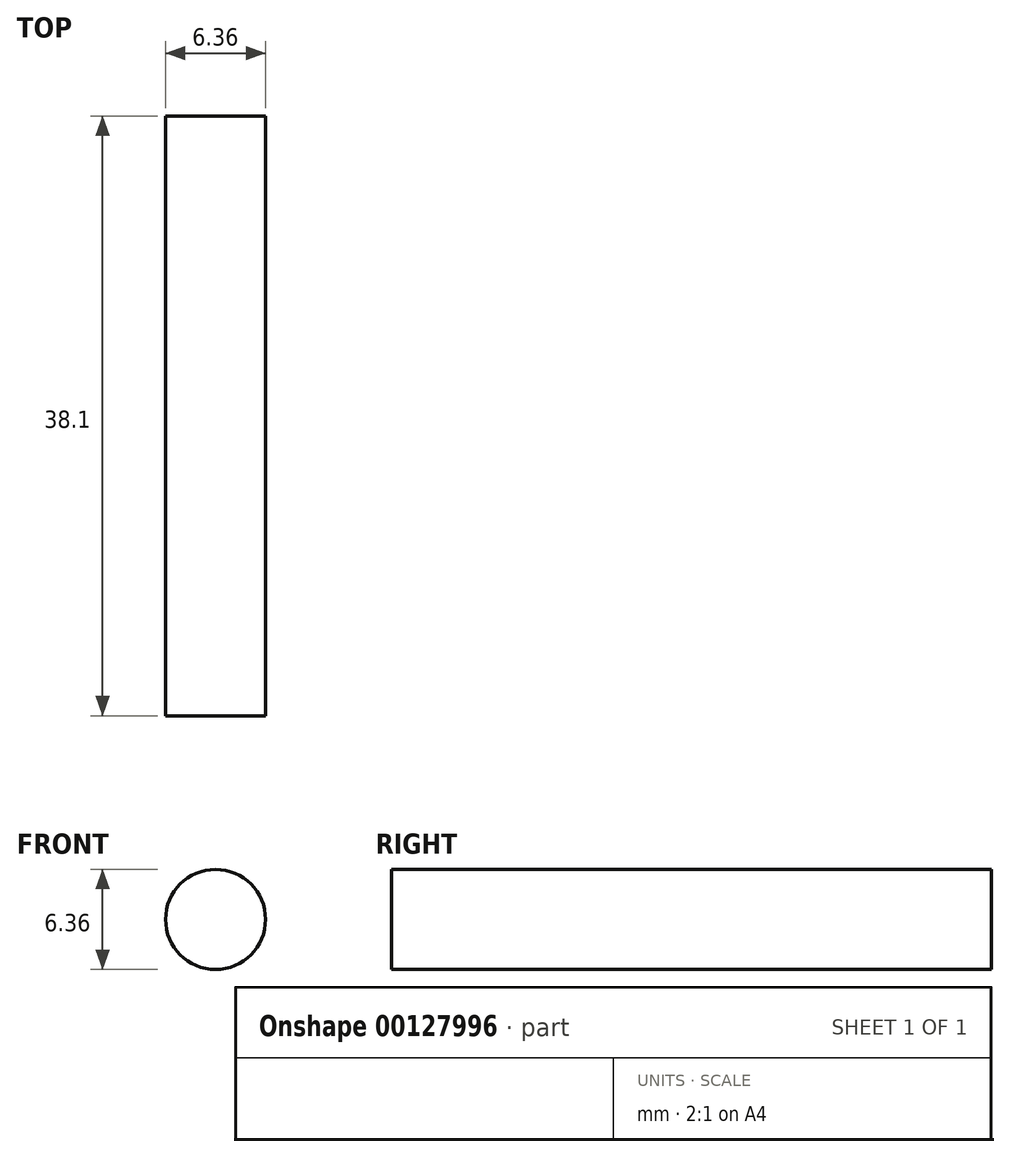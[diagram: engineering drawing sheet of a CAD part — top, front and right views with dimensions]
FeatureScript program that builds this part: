
annotation { "Feature Type Name" : "Feature", "Feature Type Description" : "" }
export const myFeature = defineFeature(function(context is Context, id is Id, definition is map)
    precondition{}
    {
        {
            var Q0;
            Q0=qCreatedBy(makeId("Front.planeOp"),FACE);
            var sketch = newSketch(context, id + "F0", { "sketchPlane" : qUnion([Q0])});
            skCircle(sketch, "E0", {"center": v(0, 0) * mm, "radius": 3.18 * mm});
            skSolve(sketch);
        }
        {
            var Q0;
            Q0 = qSketchRegion(id + "F0", true);
            extrude(context, id + "F1", {"entities" : qUnion([Q0]), "depth" : 38.1 * mm});
        }
    });
